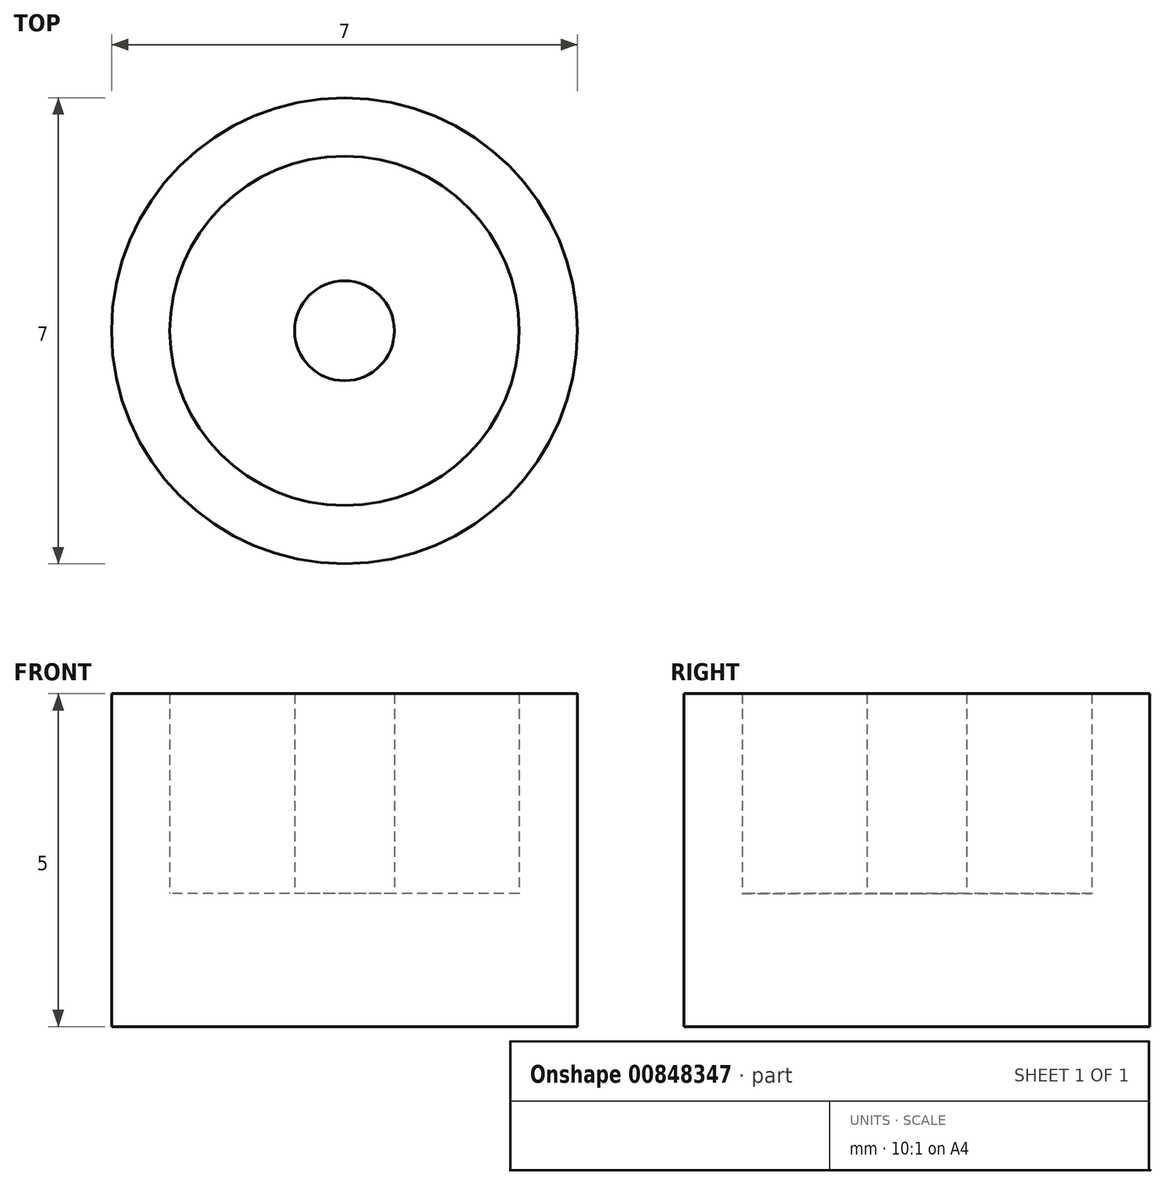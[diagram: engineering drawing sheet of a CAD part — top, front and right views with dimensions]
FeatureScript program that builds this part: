
annotation { "Feature Type Name" : "Feature", "Feature Type Description" : "" }
export const myFeature = defineFeature(function(context is Context, id is Id, definition is map)
    precondition{}
    {
        {
            var Q0;
            Q0=qCreatedBy(makeId("Top.planeOp"),FACE);
            var sketch = newSketch(context, id + "F0", { "sketchPlane" : qUnion([Q0])});
            skCircle(sketch, "E0", {"center": v(0, 0) * mm, "radius": 3.5 * mm});
            skSolve(sketch);
        }
        {
            var Q0;
            Q0 = qSketchRegion(id + "F0", true);
            extrude(context, id + "F1", {"entities" : qUnion([Q0]), "depth" : 5 * mm, "offsetDistance" : 25 * mm});
        }
        {
            var Q0;
            Q0=qCreatedBy(makeId("Top.planeOp"),FACE);
            var sketch = newSketch(context, id + "F2", { "sketchPlane" : qUnion([Q0])});
            skCircle(sketch, "E1", {"center": v(0, 0) * mm, "radius": 2.62 * mm});
            skCircle(sketch, "E2", {"center": v(0, 0) * mm, "radius": 0.75 * mm});
            skSolve(sketch);
        }
        {
            var Q0;
            Q0 = qSketchRegion(id + "F2", true);
            extrude(context, id + "F3", {"entities" : qUnion([Q0]), "operationType" : NewBodyOperationType.REMOVE, "depth" : 5 * mm, "offsetDistance" : 25 * mm, "hasSecondDirection" : true, "secondDirectionOppositeDirection" : true, "secondDirectionDepth" : -2 * mm});
        }
    });
